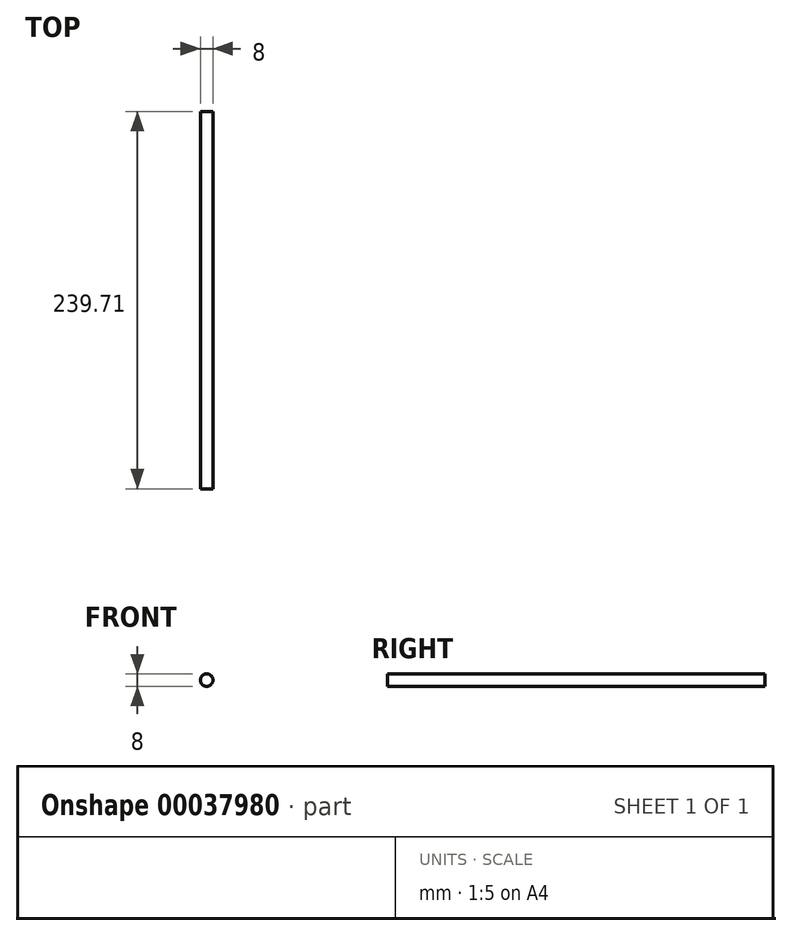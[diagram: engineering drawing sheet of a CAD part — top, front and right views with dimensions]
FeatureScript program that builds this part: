
annotation { "Feature Type Name" : "Feature", "Feature Type Description" : "" }
export const myFeature = defineFeature(function(context is Context, id is Id, definition is map)
    precondition{}
    {
        {
            var Q0;
            Q0=qCreatedBy(makeId("Front.planeOp"),FACE);
            var sketch = newSketch(context, id + "F0", { "sketchPlane" : qUnion([Q0])});
            skCircle(sketch, "E0", {"center": v(0, 0) * mm, "radius": 4 * mm});
            skSolve(sketch);
        }
        {
            var Q0;
            Q0=qSketchRegion(id+"F0",true);
            extrude(context, id + "F1", {"entities" : qUnion([Q0]), "depth" : 239.71 * mm});
        }
    });
